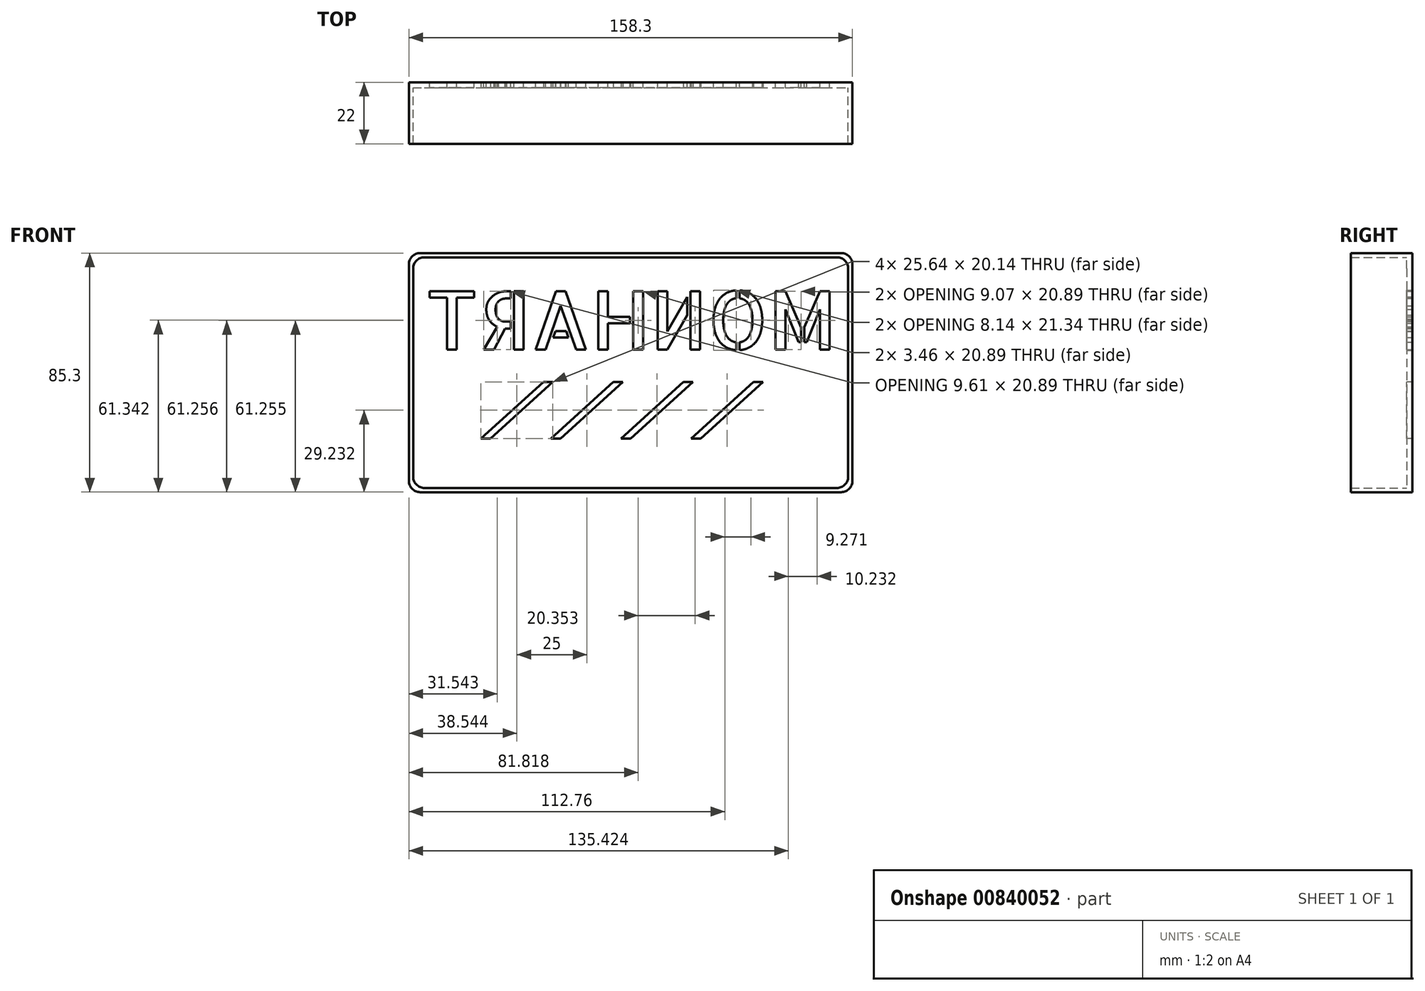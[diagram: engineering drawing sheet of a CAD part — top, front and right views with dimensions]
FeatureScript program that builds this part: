
annotation { "Feature Type Name" : "Feature", "Feature Type Description" : "" }
export const myFeature = defineFeature(function(context is Context, id is Id, definition is map)
    precondition{}
    {
        {
            var Q0;
            Q0=qCreatedBy(makeId("Front.planeOp"),FACE);
            var sketch = newSketch(context, id + "F0", { "sketchPlane" : qUnion([Q0])});
            skLineSegment(sketch, "E0.bottom", {"start": v(-70.42, 46) * mm, "end": v(79.88, 46) * mm});
            skLineSegment(sketch, "E0.top", {"start": v(-70.42, -39.3) * mm, "end": v(79.88, -39.3) * mm});
            skLineSegment(sketch, "E0.left", {"start": v(-74.42, 42) * mm, "end": v(-74.42, -35.3) * mm});
            skLineSegment(sketch, "E0.right", {"start": v(83.88, 42) * mm, "end": v(83.88, -35.3) * mm});
            skPoint(sketch, "E1.visualSharp", {"position": v(-74.42, 46) * mm});
            skArc(sketch, "E1.filletArc", {"start": v(-70.42, 46) * mm, "mid": v(-73.25, 44.83) * mm, "end": v(-74.42, 42) * mm});
            skPoint(sketch, "E2.visualSharp", {"position": v(-74.42, -39.3) * mm});
            skArc(sketch, "E2.filletArc", {"start": v(-74.42, -35.3) * mm, "mid": v(-73.25, -38.13) * mm, "end": v(-70.42, -39.3) * mm});
            skPoint(sketch, "E3.visualSharp", {"position": v(83.88, 46) * mm});
            skArc(sketch, "E3.filletArc", {"start": v(83.88, 42) * mm, "mid": v(82.7, 44.83) * mm, "end": v(79.88, 46) * mm});
            skPoint(sketch, "E4.visualSharp", {"position": v(83.88, -39.3) * mm});
            skArc(sketch, "E4.filletArc", {"start": v(79.88, -39.3) * mm, "mid": v(82.7, -38.13) * mm, "end": v(83.88, -35.3) * mm});
            skSolve(sketch);
        }
        {
            var Q0;
            Q0=makeQuery(id+"F0.imprint","IMPRINT",FACE,{"disambiguationData":[TD([[makeQuery(id+"F0.imprint","IMPRINT",EDGE,{"derivedFrom":sQuery(id+"F0.wireOp",EDGE,"E0.bottom")}),-1.0]])]});
            extrude(context, id + "F1", {"entities" : qUnion([Q0]), "depth" : 2 * mm, "offsetDistance" : 25 * mm});
        }
        {
            var Q0;
            Q0=makeQuery(id+"F1.opExtrude","CAP_FACE",FACE,{"disambiguationData":[OSD([sQuery(id+"F0.wireOp",EDGE,"E0.bottom"),sQuery(id+"F0.wireOp",EDGE,"E0.top"),sQuery(id+"F0.wireOp",EDGE,"E0.left"),sQuery(id+"F0.wireOp",EDGE,"E0.right"),sQuery(id+"F0.wireOp",EDGE,"E1.filletArc"),sQuery(id+"F0.wireOp",EDGE,"E2.filletArc"),sQuery(id+"F0.wireOp",EDGE,"E3.filletArc"),sQuery(id+"F0.wireOp",EDGE,"E4.filletArc")])],"isStart":false});
            var sketch = newSketch(context, id + "F2", { "sketchPlane" : qUnion([Q0])});
            skLineSegment(sketch, "E5.bottom", {"start": v(-68.92, 44.5) * mm, "end": v(78.38, 44.5) * mm});
            skLineSegment(sketch, "E5.top", {"start": v(-68.92, -37.8) * mm, "end": v(78.38, -37.8) * mm});
            skLineSegment(sketch, "E5.left", {"start": v(-72.92, 40.5) * mm, "end": v(-72.92, -33.8) * mm});
            skLineSegment(sketch, "E5.right", {"start": v(82.38, 40.5) * mm, "end": v(82.38, -33.8) * mm});
            skPoint(sketch, "E6.visualSharp", {"position": v(-72.92, 44.5) * mm});
            skArc(sketch, "E6.filletArc", {"start": v(-68.92, 44.5) * mm, "mid": v(-71.75, 43.33) * mm, "end": v(-72.92, 40.5) * mm});
            skPoint(sketch, "E7.visualSharp", {"position": v(-72.92, -37.8) * mm});
            skArc(sketch, "E7.filletArc", {"start": v(-72.92, -33.8) * mm, "mid": v(-71.75, -36.63) * mm, "end": v(-68.92, -37.8) * mm});
            skPoint(sketch, "E8.visualSharp", {"position": v(82.38, -37.8) * mm});
            skArc(sketch, "E8.filletArc", {"start": v(78.38, -37.8) * mm, "mid": v(81.2, -36.63) * mm, "end": v(82.38, -33.8) * mm});
            skPoint(sketch, "E9.visualSharp", {"position": v(82.38, 44.5) * mm});
            skArc(sketch, "E9.filletArc", {"start": v(82.38, 40.5) * mm, "mid": v(81.2, 43.33) * mm, "end": v(78.38, 44.5) * mm});
            skSolve(sketch);
        }
        {
            var Q0;
            Q0=makeQuery(id+"F2.imprint","IMPRINT",FACE,{"disambiguationData":[TD([[makeQuery(id+"F2.imprint","IMPRINT",EDGE,{"derivedFrom":sQuery(id+"F2.wireOp",EDGE,"E5.bottom")}),1.0]])]});
            extrude(context, id + "F3", {"entities" : qUnion([Q0]), "operationType" : NewBodyOperationType.ADD, "depth" : 20 * mm, "offsetDistance" : 25 * mm});
        }
        {
            var Q0;
            Q0=makeQuery(id+"F1.opExtrude","CAP_FACE",FACE,{"disambiguationData":[OSD([sQuery(id+"F0.wireOp",EDGE,"E0.bottom"),sQuery(id+"F0.wireOp",EDGE,"E0.top"),sQuery(id+"F0.wireOp",EDGE,"E0.left"),sQuery(id+"F0.wireOp",EDGE,"E0.right"),sQuery(id+"F0.wireOp",EDGE,"E1.filletArc"),sQuery(id+"F0.wireOp",EDGE,"E2.filletArc"),sQuery(id+"F0.wireOp",EDGE,"E3.filletArc"),sQuery(id+"F0.wireOp",EDGE,"E4.filletArc")])],"isStart":true});
            var sketch = newSketch(context, id + "F4", { "sketchPlane" : qUnion([Q0])});
            skText(sketch, "E10", { "text": "MONHART", "fontName": "AllertaStencil-Regular.ttf"});
            const initialGuessF4  = {"E10": [-0.07838, 0.01151, 1, 0, 0.0209]};
            skSetInitialGuess(sketch, initialGuessF4);
            skSolve(sketch);
        }
        {
            var Q0;
            Q0 = qSketchRegion(id + "F4", true);
            extrude(context, id + "F5", {"entities" : qUnion([Q0]), "operationType" : NewBodyOperationType.REMOVE, "oppositeDirection" : true, "depth" : 25 * mm, "offsetDistance" : 25 * mm});
        }
        {
            var Q0;
            Q0=makeQuery(id+"F1.opExtrude","CAP_FACE",FACE,{"disambiguationData":[OSD([sQuery(id+"F0.wireOp",EDGE,"E0.bottom"),sQuery(id+"F0.wireOp",EDGE,"E0.top"),sQuery(id+"F0.wireOp",EDGE,"E0.left"),sQuery(id+"F0.wireOp",EDGE,"E0.right"),sQuery(id+"F0.wireOp",EDGE,"E1.filletArc"),sQuery(id+"F0.wireOp",EDGE,"E2.filletArc"),sQuery(id+"F0.wireOp",EDGE,"E3.filletArc"),sQuery(id+"F0.wireOp",EDGE,"E4.filletArc")])],"isStart":false});
            var sketch = newSketch(context, id + "F6", { "sketchPlane" : qUnion([Q0])});
            skLineSegment(sketch, "E11", {"start": v(-48.7, -20.14) * mm, "end": v(-26.46, 0) * mm});
            skLineSegment(sketch, "E12", {"start": v(-26.46, 0) * mm, "end": v(-23.06, 0) * mm});
            skLineSegment(sketch, "E13", {"start": v(-23.06, 0) * mm, "end": v(-45.3, -20.14) * mm});
            skLineSegment(sketch, "E14", {"start": v(-45.3, -20.14) * mm, "end": v(-48.7, -20.14) * mm});
            skLineSegment(sketch, "E15", {"start": v(-56.55, -9.67) * mm, "end": v(65.9, -10.07) * mm, "construction": true});
            skPoint(sketch, "E15.endSnap0", {"position": v(-34.18, -10.07) * mm});
            skLineSegment(sketch, "E16.1.0.0", {"start": v(-23.7, -20.14) * mm, "end": v(-1.46, 0) * mm});
            skLineSegment(sketch, "E16.1.0.1", {"start": v(-1.46, 0) * mm, "end": v(1.94, 0) * mm});
            skLineSegment(sketch, "E16.1.0.2", {"start": v(1.94, 0) * mm, "end": v(-20.3, -20.14) * mm});
            skLineSegment(sketch, "E16.1.0.3", {"start": v(-20.3, -20.14) * mm, "end": v(-23.7, -20.14) * mm});
            skLineSegment(sketch, "E16.2.0.0", {"start": v(1.3, -20.14) * mm, "end": v(23.54, 0) * mm});
            skLineSegment(sketch, "E16.2.0.1", {"start": v(23.54, 0) * mm, "end": v(26.94, 0) * mm});
            skLineSegment(sketch, "E16.2.0.2", {"start": v(26.94, 0) * mm, "end": v(4.7, -20.14) * mm});
            skLineSegment(sketch, "E16.2.0.3", {"start": v(4.7, -20.14) * mm, "end": v(1.3, -20.14) * mm});
            skLineSegment(sketch, "E16.3.0.0", {"start": v(26.3, -20.14) * mm, "end": v(48.54, 0) * mm});
            skLineSegment(sketch, "E16.3.0.1", {"start": v(48.54, 0) * mm, "end": v(51.94, 0) * mm});
            skLineSegment(sketch, "E16.3.0.2", {"start": v(51.94, 0) * mm, "end": v(29.7, -20.14) * mm});
            skLineSegment(sketch, "E16.3.0.3", {"start": v(29.7, -20.14) * mm, "end": v(26.3, -20.14) * mm});
            skLineSegment(sketch, "E16.direction1", {"start": v(-48.7, -20.14) * mm, "end": v(-23.7, -20.14) * mm, "construction": true});
            skSolve(sketch);
        }
        {
            var Q0;
            Q0=makeQuery(id+"F6.imprint","IMPRINT",FACE,{"disambiguationData":[TD([[makeQuery(id+"F6.imprint","IMPRINT",EDGE,{"derivedFrom":sQuery(id+"F6.wireOp",EDGE,"E11")}),-1.0]])]});
            var Q1;
            Q1=makeQuery(id+"F6.imprint","IMPRINT",FACE,{"disambiguationData":[TD([[makeQuery(id+"F6.imprint","IMPRINT",EDGE,{"derivedFrom":sQuery(id+"F6.wireOp",EDGE,"E16.3.0.0")}),-1.0]])]});
            var Q2;
            Q2=makeQuery(id+"F6.imprint","IMPRINT",FACE,{"disambiguationData":[TD([[makeQuery(id+"F6.imprint","IMPRINT",EDGE,{"derivedFrom":sQuery(id+"F6.wireOp",EDGE,"E16.2.0.0")}),-1.0]])]});
            var Q3;
            Q3=makeQuery(id+"F6.imprint","IMPRINT",FACE,{"disambiguationData":[TD([[makeQuery(id+"F6.imprint","IMPRINT",EDGE,{"derivedFrom":sQuery(id+"F6.wireOp",EDGE,"E16.1.0.0")}),-1.0]])]});
            extrude(context, id + "F7", {"entities" : qUnion([Q0, Q1, Q2, Q3]), "operationType" : NewBodyOperationType.REMOVE, "oppositeDirection" : true, "depth" : 25 * mm, "offsetDistance" : 25 * mm});
        }
    });
